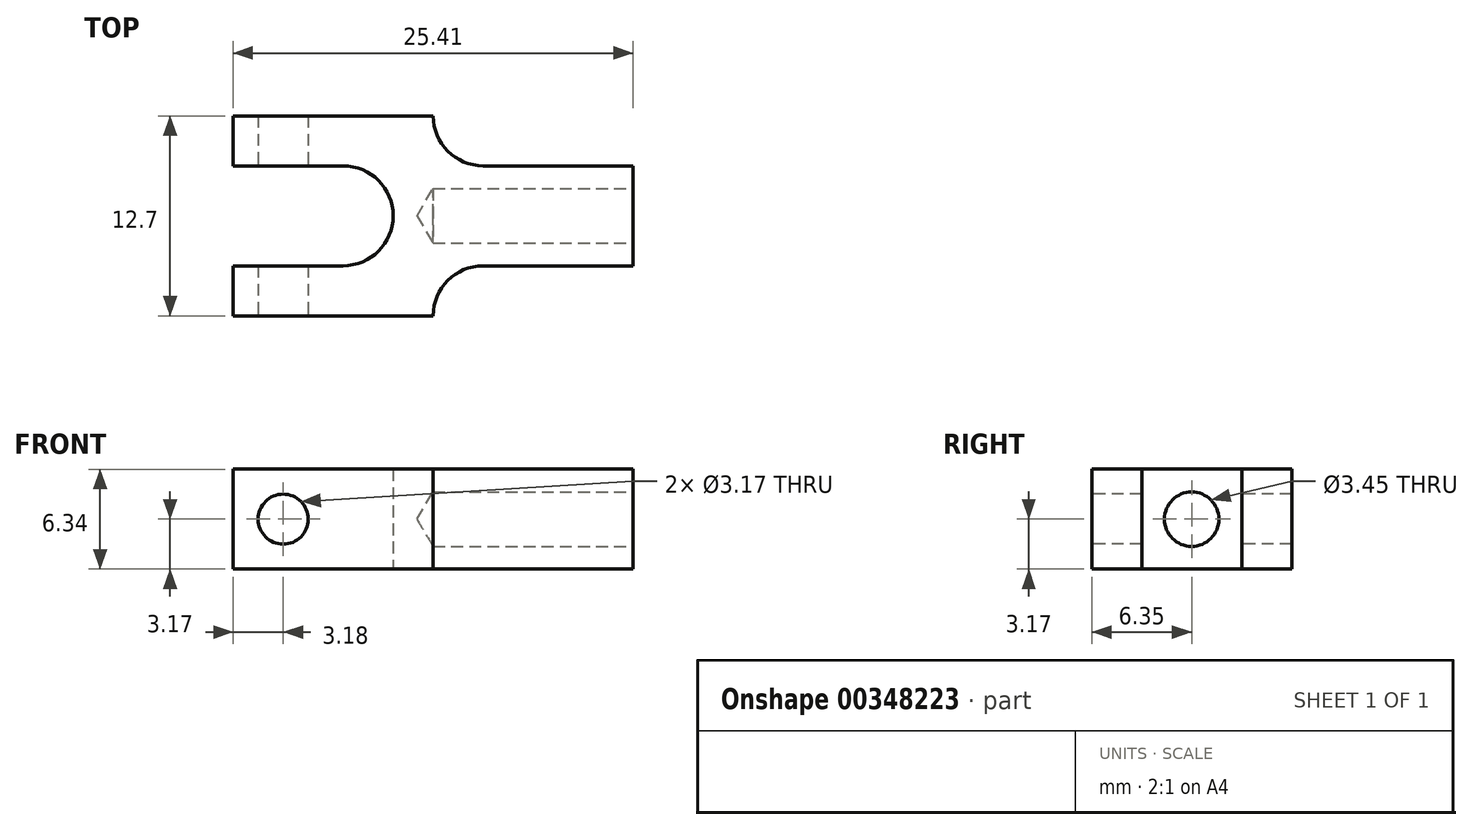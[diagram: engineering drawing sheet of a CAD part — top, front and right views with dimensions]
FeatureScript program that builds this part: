
annotation { "Feature Type Name" : "Feature", "Feature Type Description" : "" }
export const myFeature = defineFeature(function(context is Context, id is Id, definition is map)
    precondition{}
    {
        {
            var Q0;
            Q0=qCreatedBy(makeId("Top.planeOp"),FACE);
            var sketch = newSketch(context, id + "F0", { "sketchPlane" : qUnion([Q0])});
            skLineSegment(sketch, "E0", {"start": v(-6.98, -3.18) * mm, "end": v(-6.98, -6.35) * mm});
            skLineSegment(sketch, "E1", {"start": v(-6.99, -6.35) * mm, "end": v(5.72, -6.35) * mm});
            skArc(sketch, "E2", {"start": v(0, 3.18) * mm, "mid": v(3.18, 0) * mm, "end": v(0, -3.18) * mm});
            skLineSegment(sketch, "E3", {"start": v(0, -3.18) * mm, "end": v(-6.98, -3.18) * mm});
            skLineSegment(sketch, "E4", {"start": v(0, 3.18) * mm, "end": v(-6.98, 3.18) * mm});
            skLineSegment(sketch, "E5", {"start": v(-6.99, 3.18) * mm, "end": v(-6.99, 6.35) * mm});
            skLineSegment(sketch, "E6", {"start": v(-6.98, 6.35) * mm, "end": v(5.72, 6.35) * mm});
            skLineSegment(sketch, "E7", {"start": v(8.9, -3.18) * mm, "end": v(18.41, -3.18) * mm});
            skLineSegment(sketch, "E8", {"start": v(18.41, -3.18) * mm, "end": v(18.41, 3.18) * mm});
            skLineSegment(sketch, "E9", {"start": v(18.41, 3.18) * mm, "end": v(8.9, 3.18) * mm});
            skPoint(sketch, "E10", {"position": v(18.41, 0) * mm});
            skArc(sketch, "E11", {"start": v(8.9, 3.17) * mm, "mid": v(6.64, 4.1) * mm, "end": v(5.72, 6.35) * mm});
            skArc(sketch, "E12", {"start": v(8.9, -3.18) * mm, "mid": v(6.64, -4.1) * mm, "end": v(5.72, -6.35) * mm});
            skSolve(sketch);
        }
        {
            var Q0;
            Q0=qSketchRegion(id+"F0",true);
            extrude(context, id + "F1", {"entities" : qUnion([Q0]), "endBound" : BoundingType.SYMMETRIC, "depth" : 6.35 * mm});
        }
        {
            var Q0;
            Q0=makeQuery(id+"F1.opExtrude","SWEPT_FACE",FACE,{"disambiguationData":[OSD([sQuery(id+"F0.wireOp",EDGE,"E8")])]});
            var sketch = newSketch(context, id + "F2", { "sketchPlane" : qUnion([Q0])});
            skPoint(sketch, "E13", {"position": v(0, 0) * mm});
            skSolve(sketch);
        }
        {
            var Q0;
            Q0=sQuery(id+"F2.wireOp",VERTEX,"E13");
            var Q1;
            Q1=makeQuery(id+"F1.opExtrude","SWEPT_BODY",BODY,{"disambiguationData":[OSD([sQuery(id+"F0.wireOp",EDGE,"E0"),sQuery(id+"F0.wireOp",EDGE,"E1"),sQuery(id+"F0.wireOp",EDGE,"E2"),sQuery(id+"F0.wireOp",EDGE,"E3"),sQuery(id+"F0.wireOp",EDGE,"E4"),sQuery(id+"F0.wireOp",EDGE,"E5"),sQuery(id+"F0.wireOp",EDGE,"E6"),sQuery(id+"F0.wireOp",EDGE,"E7"),sQuery(id+"F0.wireOp",EDGE,"E8"),sQuery(id+"F0.wireOp",EDGE,"E9"),sQuery(id+"F0.wireOp",EDGE,"E11"),sQuery(id+"F0.wireOp",EDGE,"E12")])]});
            hole(context, id + "F3", {"style" : HoleStyle.SIMPLE, "holeDiameter" : 3.45 * mm, "endStyle" : HoleEndStyle.BLIND, "holeDepth" : 12.7 * mm, "locations" : qUnion([Q0]), "scope" : qUnion([Q1])});
        }
        {
            var Q0;
            Q0=makeQuery(id+"F1.opExtrude","SWEPT_FACE",FACE,{"disambiguationData":[OSD([sQuery(id+"F0.wireOp",EDGE,"E1")])]});
            var sketch = newSketch(context, id + "F4", { "sketchPlane" : qUnion([Q0])});
            skPoint(sketch, "E14", {"position": v(-3.81, 0) * mm});
            skSolve(sketch);
        }
        {
            var Q0;
            Q0=sQuery(id+"F4.wireOp",VERTEX,"E14");
            var Q1;
            Q1=makeQuery(id+"F1.opExtrude","SWEPT_BODY",BODY,{"disambiguationData":[OSD([sQuery(id+"F0.wireOp",EDGE,"E0"),sQuery(id+"F0.wireOp",EDGE,"E1"),sQuery(id+"F0.wireOp",EDGE,"E2"),sQuery(id+"F0.wireOp",EDGE,"E3"),sQuery(id+"F0.wireOp",EDGE,"E4"),sQuery(id+"F0.wireOp",EDGE,"E5"),sQuery(id+"F0.wireOp",EDGE,"E6"),sQuery(id+"F0.wireOp",EDGE,"E7"),sQuery(id+"F0.wireOp",EDGE,"E8"),sQuery(id+"F0.wireOp",EDGE,"E9"),sQuery(id+"F0.wireOp",EDGE,"E11"),sQuery(id+"F0.wireOp",EDGE,"E12")])]});
            hole(context, id + "F5", {"style" : HoleStyle.SIMPLE, "holeDiameter" : 3.17 * mm, "endStyle" : HoleEndStyle.THROUGH, "locations" : qUnion([Q0]), "scope" : qUnion([Q1])});
        }
    });
